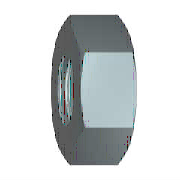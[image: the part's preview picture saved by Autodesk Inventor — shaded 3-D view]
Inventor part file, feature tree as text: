
AUTODESK INVENTOR PART (.ipt)
format: ipt  version: 2016 (Build 200138000, 138)  size: 162,816 bytes
history: native  units: mm (DEFAULTED — no unit token found)
features: sketch x3, chamfer x1, hole x1, other x1, plane x1
ambient origin geometry x7: Origin, YZ Plane, XZ Plane, X Axis, Y Axis, Z Axis, Center Point
bodies: Solid1 (feature_tree), Body (feature_tree)
feature tree (7):
  chamfer  "Chamfer1"  Angle=30.0deg  [1 undecoded]
  hole  "Thread"  [1 undecoded]
  other  "Work Axis1"
  plane  "Work Plane1"
  sketch  "Sketch1"  dims[d0=19.629909mm]
  sketch  "Sketch2"  dims[d1=8.0mm]
  sketch  "Sketch3"  dims[d2=0.0mm d3=30.0deg d4=30.0deg d5=15.3mm d6=15.3mm d7=90.0deg d25=8.376mm d26=6.0mm d27=4.0mm d28=2.0mm d29=14.3117mm d30=8.0mm d31=20.594885mm d8=0.811899mm d9=30.0deg d10=0.811899mm d11=30.0deg d13=0.0mm d14=0.0mm d39=0.0mm d40=0.811899mm d41=0.811899mm d42=0.0mm]
note: 2 required parameter values undecoded (feature->parameter linkage not recoverable at this tier; creation-order binding heuristic only, values carry confidence <= 0.55)
